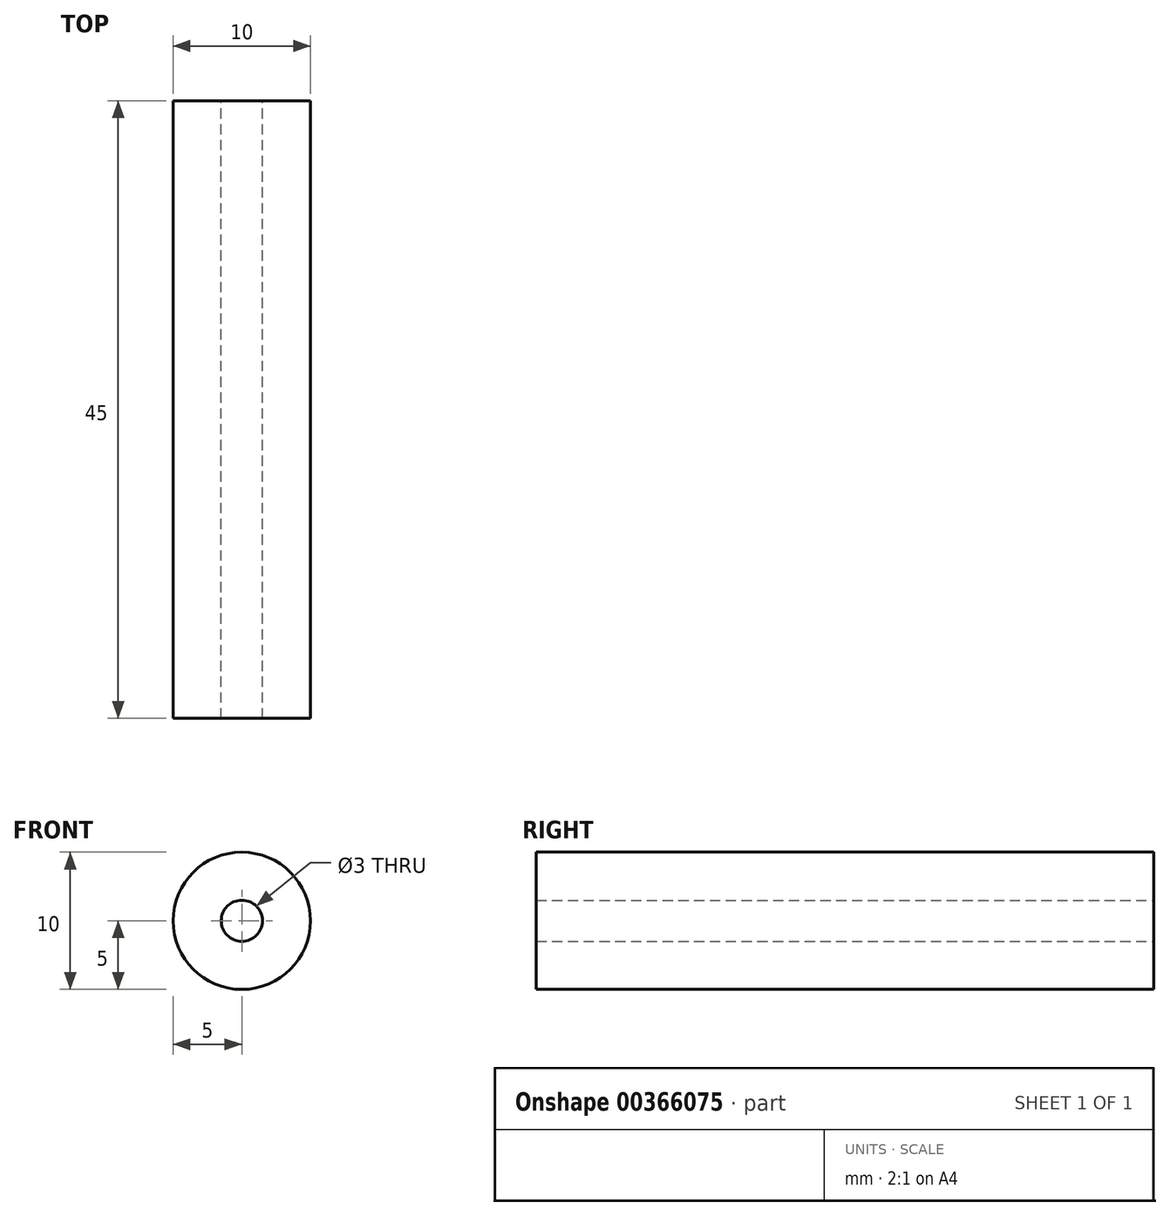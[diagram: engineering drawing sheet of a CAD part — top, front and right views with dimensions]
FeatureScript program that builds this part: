
annotation { "Feature Type Name" : "Feature", "Feature Type Description" : "" }
export const myFeature = defineFeature(function(context is Context, id is Id, definition is map)
    precondition{}
    {
        {
            var Q0;
            Q0=qCreatedBy(makeId("Front.planeOp"),FACE);
            var sketch = newSketch(context, id + "F0", { "sketchPlane" : qUnion([Q0])});
            skCircle(sketch, "E0", {"center": v(0, 0) * mm, "radius": 5 * mm});
            skSolve(sketch);
        }
        {
            var Q0;
            Q0=makeQuery(id+"F0.imprint","IMPRINT",FACE,{"disambiguationData":[TD([[makeQuery(id+"F0.imprint","IMPRINT",EDGE,{"derivedFrom":sQuery(id+"F0.wireOp",EDGE,"E0")}),1.0]])]});
            extrude(context, id + "F1", {"entities" : qUnion([Q0]), "depth" : 45 * mm});
        }
        {
            var Q0;
            Q0=qCreatedBy(makeId("Front.planeOp"),FACE);
            var sketch = newSketch(context, id + "F2", { "sketchPlane" : qUnion([Q0])});
            skCircle(sketch, "E1", {"center": v(0, 0) * mm, "radius": 1.5 * mm});
            skSolve(sketch);
        }
        {
            var Q0;
            Q0=sQuery(id+"F2.wireOp",VERTEX,"E1.center");
            var Q1;
            Q1=makeQuery(id+"F1.opExtrude","SWEPT_BODY",BODY,{"disambiguationData":[OSD([sQuery(id+"F0.wireOp",EDGE,"E0")])]});
            hole(context, id + "F3", {"style" : HoleStyle.SIMPLE, "endStyle" : HoleEndStyle.THROUGH, "oppositeDirection" : true, "holeDiameter" : 3 * mm, "isTappedThrough" : true, "tappedDepth" : 12 * mm, "tapClearance" : 3, "locations" : qUnion([Q0]), "scope" : qUnion([Q1])});
        }
    });
